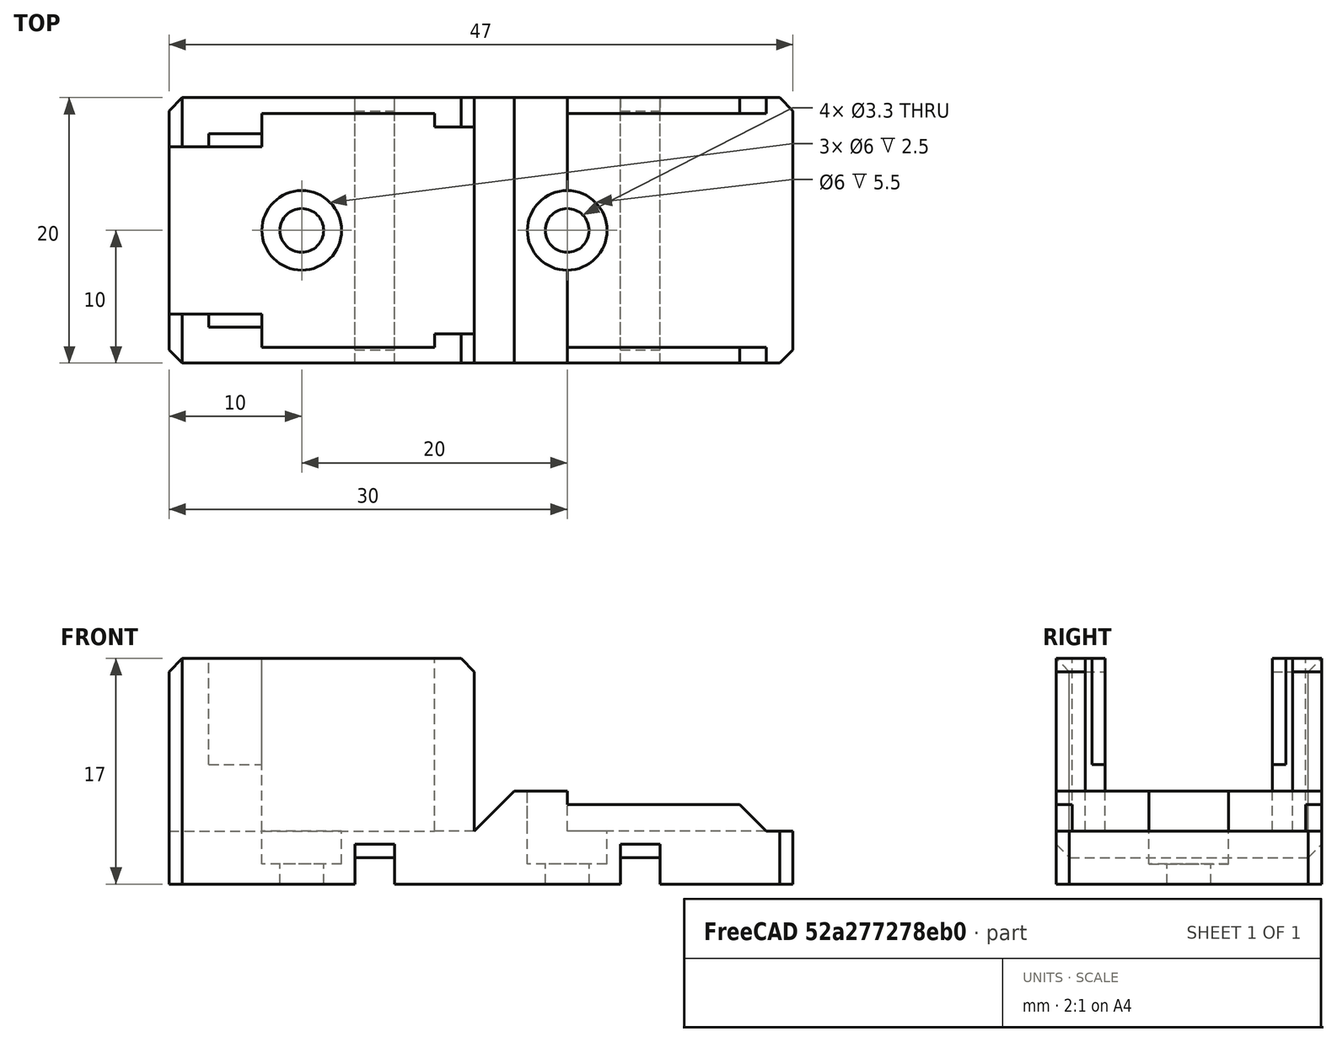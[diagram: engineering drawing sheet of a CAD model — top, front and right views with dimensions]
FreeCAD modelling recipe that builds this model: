
FCSTD DOCUMENT  (FreeCAD 0.18R14555 (Git shallow))
Label: bear-power-connector
License: All rights reserved
LicenseURL: http://en.wikipedia.org/wiki/All_rights_reserved
objects: Part::Box×14, Part::Cut×7, Part::Cylinder×5, Part::Chamfer×4, Part::MultiFuse×3, Part::Feature×1
note: 34 computed .brp shape members not serialized (recipe doc carries the construction recipe); baked Part::Feature solids carry a one-line shape summary decoded from their .brp

FEATURE [Part::Box] Box  label="Cube"
  AttacherType = Attacher::AttachEngine3D
  Height = 4
  Length = 47
  Width = 20
FEATURE [Part::Box] Box002  label="Cube002"
  AttacherType = Attacher::AttachEngine3D
  Height = 17
  Length = 13
  Placement = pos=(7,18.8,0) rot=(0,0,1;0rad)
  Width = 1.2
FEATURE [Part::Box] Box003  label="Cube003"
  AttacherType = Attacher::AttachEngine3D
  Height = 17
  Length = 7
  Placement = pos=(8,0,0) rot=(0,0,1;0rad)
  Width = 3.7
FEATURE [Part::Box] Box004  label="Cube004"
  AttacherType = Attacher::AttachEngine3D
  Height = 17
  Length = 7
  Placement = pos=(8,16.3,0) rot=(0,0,1;0rad)
  Width = 3.7
FEATURE [Part::Box] Box005  label="Cube005"
  AttacherType = Attacher::AttachEngine3D
  Height = 8
  Length = 4
  Placement = pos=(11,2.7,9) rot=(0,0,1;0rad)
  Width = 1
FEATURE [Part::Box] Box006  label="Cube006"
  AttacherType = Attacher::AttachEngine3D
  Height = 8
  Length = 4
  Placement = pos=(11,16.3,9) rot=(0,0,1;0rad)
  Width = 1
FEATURE [Part::Box] Box007  label="Cube007"
  AttacherType = Attacher::AttachEngine3D
  Height = 17
  Length = 13
  Placement = pos=(7,-2.1e-15,0) rot=(0,0,1;0rad)
  Width = 1.2
FEATURE [Part::Box] Box008  label="Cube008"
  AttacherType = Attacher::AttachEngine3D
  Height = 7
  Length = 7
  Placement = pos=(31,0,0) rot=(0,0,1;0rad)
  Width = 20
FEATURE [Part::Box] Box009  label="Cube009"
  AttacherType = Attacher::AttachEngine3D
  Height = 17
  Length = 3
  Placement = pos=(20,17.8,0) rot=(0,0,1;0rad)
  Width = 2.2
FEATURE [Part::Box] Box010  label="Cube010"
  AttacherType = Attacher::AttachEngine3D
  Height = 17
  Length = 3
  Placement = pos=(20,-2.1e-15,0) rot=(0,0,1;0rad)
  Width = 2.2
FEATURE [Part::Box] Box011  label="Cube011"
  AttacherType = Attacher::AttachEngine3D
  Height = 6
  Length = 15
  Placement = pos=(38,18.8,0) rot=(0,0,1;0rad)
  Width = 1.2
FEATURE [Part::Box] Box012  label="Cube012"
  AttacherType = Attacher::AttachEngine3D
  Height = 6
  Length = 15
  Placement = pos=(38,-2.1e-15,0) rot=(0,0,1;0rad)
  Width = 1.2
FEATURE [Part::Cut] Cut
  Base = -> Box004
  Placement = pos=(-8,0,0) rot=(0,0,1;0rad)
  Tool = -> Box006
FEATURE [Part::Cut] Cut001
  Base = -> Box003
  Placement = pos=(-8,0,0) rot=(0,0,1;0rad)
  Tool = -> Box005
FEATURE [Part::Cylinder] Cylinder
  Angle = 360
  AttacherType = Attacher::AttachEngine3D
  Height = 2.5
  Placement = pos=(10,10,0) rot=(0,0,1;0rad)
  Radius = 3
FEATURE [Part::Cylinder] Cylinder001
  Angle = 360
  AttacherType = Attacher::AttachEngine3D
  Height = 2.5
  Placement = pos=(30,10,0) rot=(0,0,1;0rad)
  Radius = 3
FEATURE [Part::Cylinder] Cylinder003
  Angle = 360
  AttacherType = Attacher::AttachEngine3D
  Height = 10
  Placement = pos=(10,10,0) rot=(0,0,1;0rad)
  Radius = 1.65
FEATURE [Part::Cylinder] Cylinder004
  Angle = 360
  AttacherType = Attacher::AttachEngine3D
  Height = 10
  Placement = pos=(30,10,0) rot=(0,0,1;0rad)
  Radius = 1.65
FEATURE [Part::Cylinder] Cylinder006
  Angle = 360
  AttacherType = Attacher::AttachEngine3D
  Height = 5.5
  Placement = pos=(30,10,4) rot=(0,0,1;0rad)
  Radius = 3
FEATURE [Part::Box] Box013  label="Cube013"
  AttacherType = Attacher::AttachEngine3D
  Height = 2
  Length = 3
  Placement = pos=(14,0,0) rot=(0,0,1;0rad)
  Width = 20
FEATURE [Part::Box] Box014  label="Cube014"
  AttacherType = Attacher::AttachEngine3D
  Height = 2
  Length = 3
  Placement = pos=(34,0,0) rot=(0,0,1;0rad)
  Width = 20
FEATURE [Part::Chamfer] Chamfer
  Base = -> Box008
  Edges = 1 edges r=3: [Edge2]
  Placement = pos=(-8,0,0) rot=(0,0,1;0rad)
FEATURE [Part::Chamfer] Chamfer001
  Base = -> Box011
  Edges = 1 edges r=2: [Edge6]
  Placement = pos=(-8,0,0) rot=(0,0,1;0rad)
FEATURE [Part::Chamfer] Chamfer002
  Base = -> Box012
  Edges = 1 edges r=2: [Edge6]
  Placement = pos=(-8,0,0) rot=(0,0,1;0rad)
FEATURE [Part::MultiFuse] Fusion005
  Shapes = -> [Cut001,Box007,Box002,Box,Box009,Chamfer,Cut,Box010,Chamfer002,Chamfer001]
FEATURE [Part::MultiFuse] Fusion
  Shapes = -> [Cylinder003,Cylinder004]
FEATURE [Part::Cut] Cut013
  Base = -> Fusion005
  Tool = -> Fusion
FEATURE [Part::MultiFuse] Fusion006
  Placement = pos=(0,0,1.5) rot=(0,0,1;0rad)
  Shapes = -> [Cylinder,Cylinder001]
FEATURE [Part::Cut] Cut014
  Base = -> Cut013
  Tool = -> Fusion006
FEATURE [Part::Cut] Cut015
  Base = -> Cut014
  Tool = -> Cylinder006
FEATURE [Part::Cut] Cut016
  Base = -> Cut015
  Tool = -> Box013
FEATURE [Part::Cut] Cut017
  Base = -> Cut016
  Tool = -> Box014
FEATURE [Part::Chamfer] Chamfer003
  Base = -> Cut017
  Edges = 14 edges r=1: [Edge19,Edge25,Edge37,Edge55,Edge56,Edge72,Edge133,Edge134,Edge151,Edge159,Edge168,Edge177,Edge199,Edge217]
FEATURE [Part::Feature] Chamfer003001  label="Chamfer004"
  shape: bbox 47 x 20 x 17 mm, 63 faces (baked)
